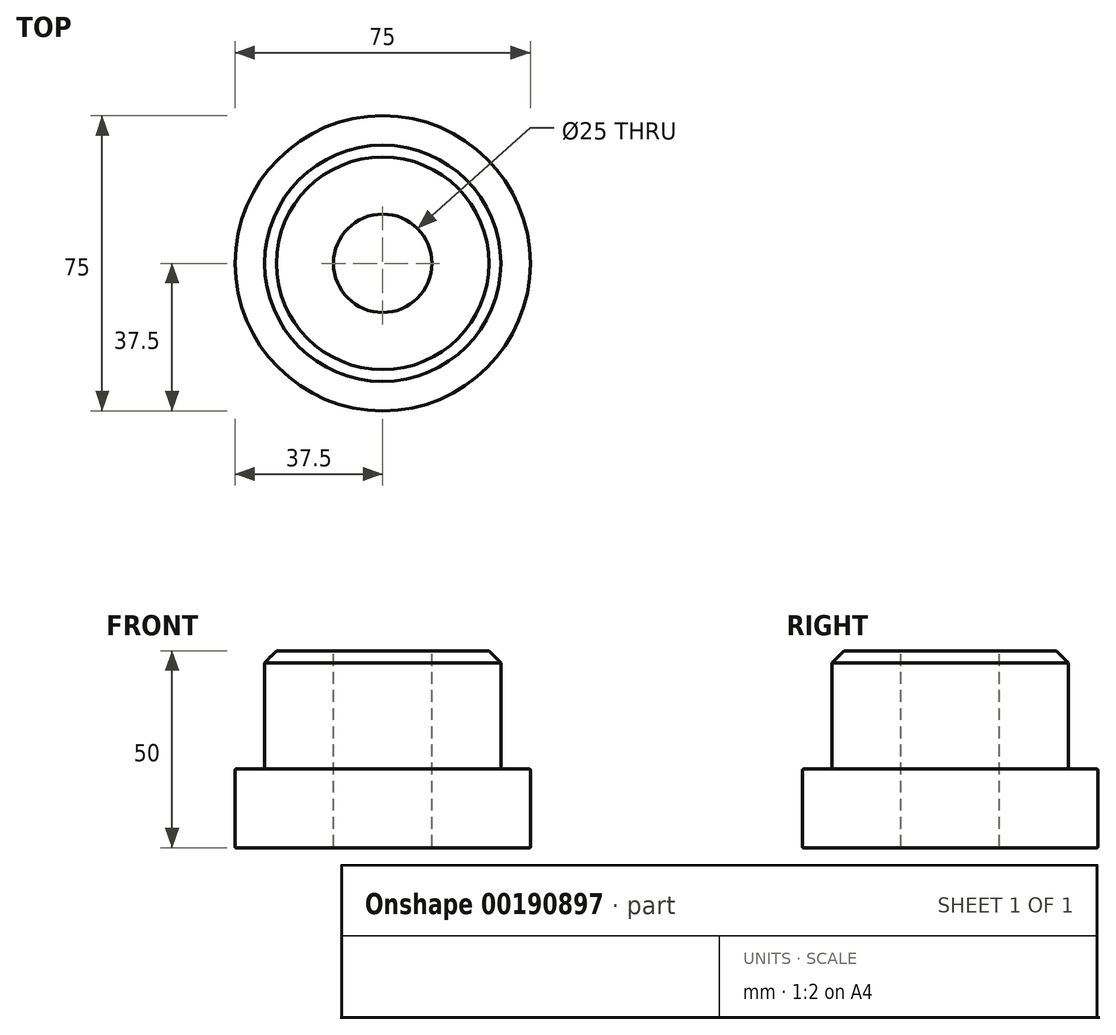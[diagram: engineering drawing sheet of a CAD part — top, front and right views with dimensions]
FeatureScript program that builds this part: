
annotation { "Feature Type Name" : "Feature", "Feature Type Description" : "" }
export const myFeature = defineFeature(function(context is Context, id is Id, definition is map)
    precondition{}
    {
        {
            var Q0;
            Q0=qCreatedBy(makeId("Front.planeOp"),FACE);
            var sketch = newSketch(context, id + "F0", { "sketchPlane" : qUnion([Q0])});
            skLineSegment(sketch, "E0", {"start": v(12.5, 50) * mm, "end": v(12.5, 0) * mm});
            skLineSegment(sketch, "E1", {"start": v(12.5, 0) * mm, "end": v(37.5, 0) * mm});
            skLineSegment(sketch, "E2", {"start": v(37.5, 0) * mm, "end": v(37.5, 20) * mm});
            skLineSegment(sketch, "E3", {"start": v(37.5, 20) * mm, "end": v(30, 20) * mm});
            skLineSegment(sketch, "E4", {"start": v(30, 20) * mm, "end": v(30, 50) * mm});
            skLineSegment(sketch, "E5", {"start": v(30, 50) * mm, "end": v(12.5, 50) * mm});
            skLineSegment(sketch, "E6", {"start": v(0, 55.54) * mm, "end": v(0, -22.78) * mm, "construction": true});
            skSolve(sketch);
        }
        {
            var Q0;
            Q0 = qSketchRegion(id + "F0", true);
            var Q1;
            Q1=sQuery(id+"F0.wireOp",EDGE,"E6");
            revolve(context, id + "F1", {"surfaceOperationType" : NewSurfaceOperationType.NEW, "entities" : qUnion([Q0]), "axis" : qUnion([Q1]), "revolveType" : RevolveType.FULL});
        }
        {
            var Q0;
            Q0=makeQuery(id+"F1.opRevolve","SWEPT_FACE",FACE,{"disambiguationData":[OSD([sQuery(id+"F0.wireOp",EDGE,"E0")])]});
            var Q1;
            Q1=makeQuery(id+"F1.opRevolve","SWEPT_FACE",FACE,{"disambiguationData":[OSD([sQuery(id+"F0.wireOp",EDGE,"E3")])]});
            var Q2;
            Q2=makeQuery(id+"F1.opRevolve","SWEPT_FACE",FACE,{"disambiguationData":[OSD([sQuery(id+"F0.wireOp",EDGE,"E1")])]});
            fillet(context, id + "F2", {"entities" : qUnion([Q0, Q1, Q2]), "radius" : 0.25 * mm, "tangentPropagation" : true, "allowEdgeOverflow" : false});
        }
        {
            var Q0;
            Q0=makeQuery(id+"F1.opRevolve","SWEPT_EDGE",EDGE,{"disambiguationData":[OSD([sQuery(id+"F0.wireOp",EDGE,"E4"),sQuery(id+"F0.wireOp",EDGE,"E5")])]});
            chamfer(context, id + "F3", {"entities" : qUnion([Q0]), "width" : 3 * mm, "tangentPropagation" : true});
        }
    });
